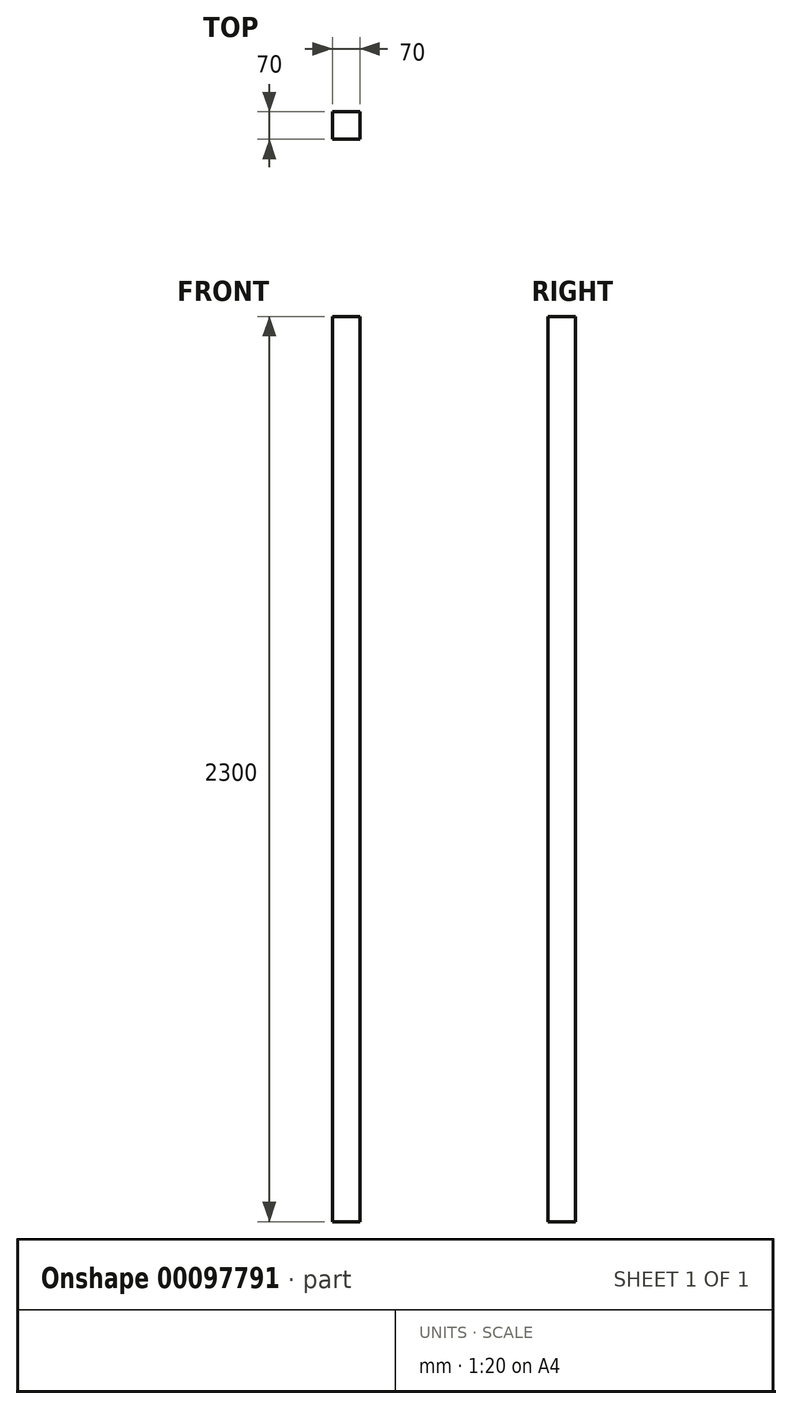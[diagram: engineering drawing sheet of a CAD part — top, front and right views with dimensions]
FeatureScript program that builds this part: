
annotation { "Feature Type Name" : "Feature", "Feature Type Description" : "" }
export const myFeature = defineFeature(function(context is Context, id is Id, definition is map)
    precondition{}
    {
        {
            var Q0;
            Q0=qCreatedBy(makeId("Top.planeOp"),FACE);
            var sketch = newSketch(context, id + "F0", { "sketchPlane" : qUnion([Q0])});
            skLineSegment(sketch, "E0.bottom", {"start": v(0, 0) * mm, "end": v(70, 0) * mm});
            skLineSegment(sketch, "E0.top", {"start": v(0, 70) * mm, "end": v(70, 70) * mm});
            skLineSegment(sketch, "E0.left", {"start": v(0, 0) * mm, "end": v(0, 70) * mm});
            skLineSegment(sketch, "E0.right", {"start": v(70, 0) * mm, "end": v(70, 70) * mm});
            skSolve(sketch);
        }
        {
            var Q0;
            Q0 = qSketchRegion(id + "F0", true);
            extrude(context, id + "F1", {"entities" : qUnion([Q0]), "depth" : 2300 * mm});
        }
    });
